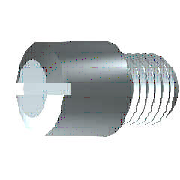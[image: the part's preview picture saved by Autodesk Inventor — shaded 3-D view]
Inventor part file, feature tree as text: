
AUTODESK INVENTOR PART (.ipt)
format: ipt  version: 2019 (Build 230136000, 136)  size: 175,104 bytes
history: native  units: mm (DEFAULTED — no unit token found)
features: sketch x2, extrude x1, other x1, plane x1
ambient origin geometry x7: Origin, YZ Plane, XZ Plane, X Axis, Y Axis, Z Axis, Center Point
bodies: Solid1 (feature_tree), Body (feature_tree)
feature tree (5):
  sketch  "Sketch1"  dims[d0=5.0mm d1=8.0mm]
  extrude  "Slot"  Depth=8.0mm
  other  "Groove1"
  plane  "Work Plane1"
  sketch  "Sketch2"  dims[d2=6.0mm d3=8.0mm d4=90.0deg d5=1.0mm d6=2.0mm d7=0.0mm d8=1.0mm d9=45.0deg d10=8.0mm d11=0.0mm d12=0.61345mm d13=0.61345mm d14=1.0mm d15=1.0mm d16=90.0deg d18=0.0mm d19=1.0mm d20=45.0deg d21=0.0mm d23=0.0mm]
